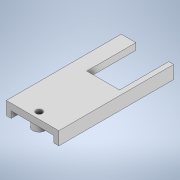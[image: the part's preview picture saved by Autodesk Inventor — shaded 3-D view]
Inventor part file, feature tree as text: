
AUTODESK INVENTOR PART (.ipt)
format: ipt  version: 2021 (Build 250183000, 183)  size: 131,072 bytes
history: native  units: mm
features: extrude x2, sketch x2, projected_geometry x1
ambient origin geometry x8: Origin, YZ Plane, XZ Plane, XY Plane, X Axis, Y Axis, Z Axis, Center Point
bodies: Volumenkörper1 (feature_tree)
feature tree (5):
  extrude  "Extrusion1"  Depth=16.0mm
  extrude  "Extrusion2"  Depth=2.0mm
  sketch  "Skizze1"  dims[d0=16.0mm d1=1.9mm]
  sketch  "Skizze2"  dims[d2=2.0mm d4=33.0mm d5=15.0mm d6=10.0mm d7=4.5mm d8=2.0mm d9=0.0mm d10=1.0mm d11=1.5mm d12=2.0mm d13=0.0mm]
  projected_geometry  "Projizierte Kontur1"
